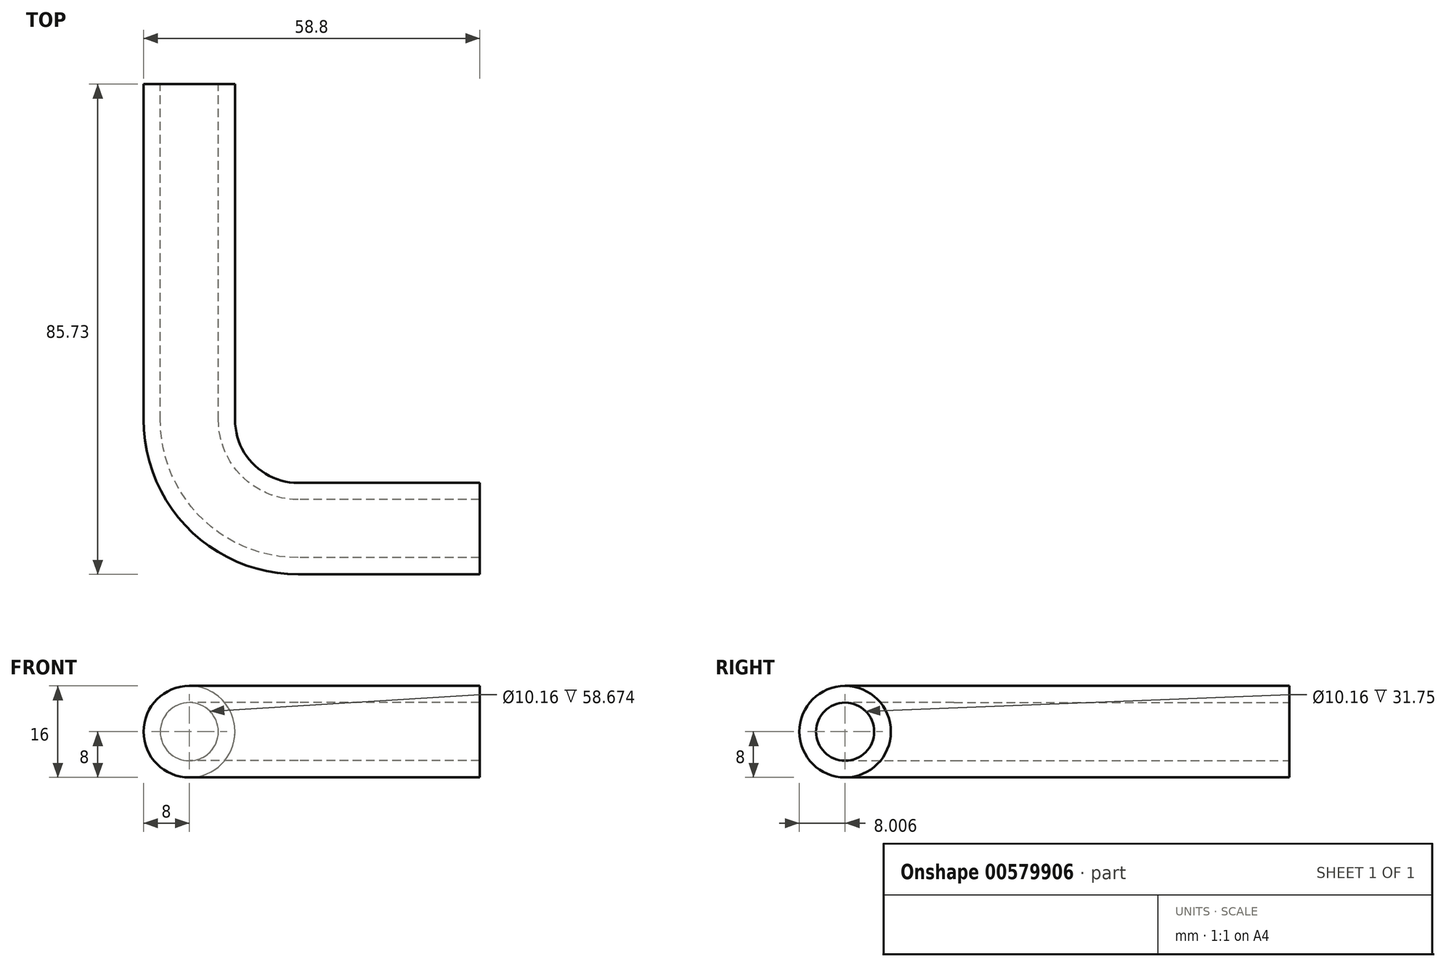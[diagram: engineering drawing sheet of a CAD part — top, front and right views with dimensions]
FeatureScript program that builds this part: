
annotation { "Feature Type Name" : "Feature", "Feature Type Description" : "" }
export const myFeature = defineFeature(function(context is Context, id is Id, definition is map)
    precondition{}
    {
        {
            var Q0;
            Q0=qCreatedBy(makeId("Front.planeOp"),FACE);
            var sketch = newSketch(context, id + "F0", { "sketchPlane" : qUnion([Q0])});
            skCircle(sketch, "E0", {"center": v(0, 0) * mm, "radius": 8 * mm});
            skCircle(sketch, "E1", {"center": v(0, 0) * mm, "radius": 5.08 * mm});
            skSolve(sketch);
        }
        {
            var Q0;
            Q0=qSketchRegion(id+"F0",true);
            extrude(context, id + "F1", {"entities" : qUnion([Q0]), "depth" : 58.67 * mm, "offsetDistance" : 25.4 * mm});
        }
        {
            var Q0;
            Q0=makeQuery(id+"F1.opExtrude","CAP_FACE",FACE,{"disambiguationData":[OSD([sQuery(id+"F0.wireOp",EDGE,"E0"),sQuery(id+"F0.wireOp",EDGE,"E1")])],"isStart":false});
            var sketch = newSketch(context, id + "F2", { "sketchPlane" : qUnion([Q0])});
            skCircle(sketch, "E2", {"center": v(0, 0) * mm, "radius": 8 * mm});
            skCircle(sketch, "E3", {"center": v(0, 0) * mm, "radius": 5.08 * mm});
            skLineSegment(sketch, "E4", {"start": v(19.05, 11.5) * mm, "end": v(19.05, -12.67) * mm});
            skSolve(sketch);
        }
        {
            var Q0;
            Q0 = qSketchRegion(id + "F2", true);
            var Q1;
            Q1=sQuery(id+"F2.wireOp",EDGE,"E4");
            revolve(context, id + "F3", {"operationType" : NewBodyOperationType.ADD, "entities" : qUnion([Q0]), "axis" : qUnion([Q1]), "revolveType" : RevolveType.ONE_DIRECTION, "oppositeDirection" : true, "angle" : 90 * degree});
        }
        {
            var Q0;
            Q0=makeQuery(id+"F3.opRevolve","CAP_FACE",FACE,{"disambiguationData":[OSD([sQuery(id+"F2.wireOp",EDGE,"E2"),sQuery(id+"F2.wireOp",EDGE,"E3")])],"isStart":false});
            var sketch = newSketch(context, id + "F4", { "sketchPlane" : qUnion([Q0])});
            skCircle(sketch, "E5", {"center": v(-77.72, 0) * mm, "radius": 8 * mm});
            skCircle(sketch, "E6", {"center": v(-77.72, 0) * mm, "radius": 5.08 * mm});
            skSolve(sketch);
        }
        {
            var Q0;
            Q0 = qSketchRegion(id + "F4", true);
            extrude(context, id + "F5", {"entities" : qUnion([Q0]), "operationType" : NewBodyOperationType.ADD, "depth" : 31.75 * mm, "offsetDistance" : 25.4 * mm});
        }
    });
